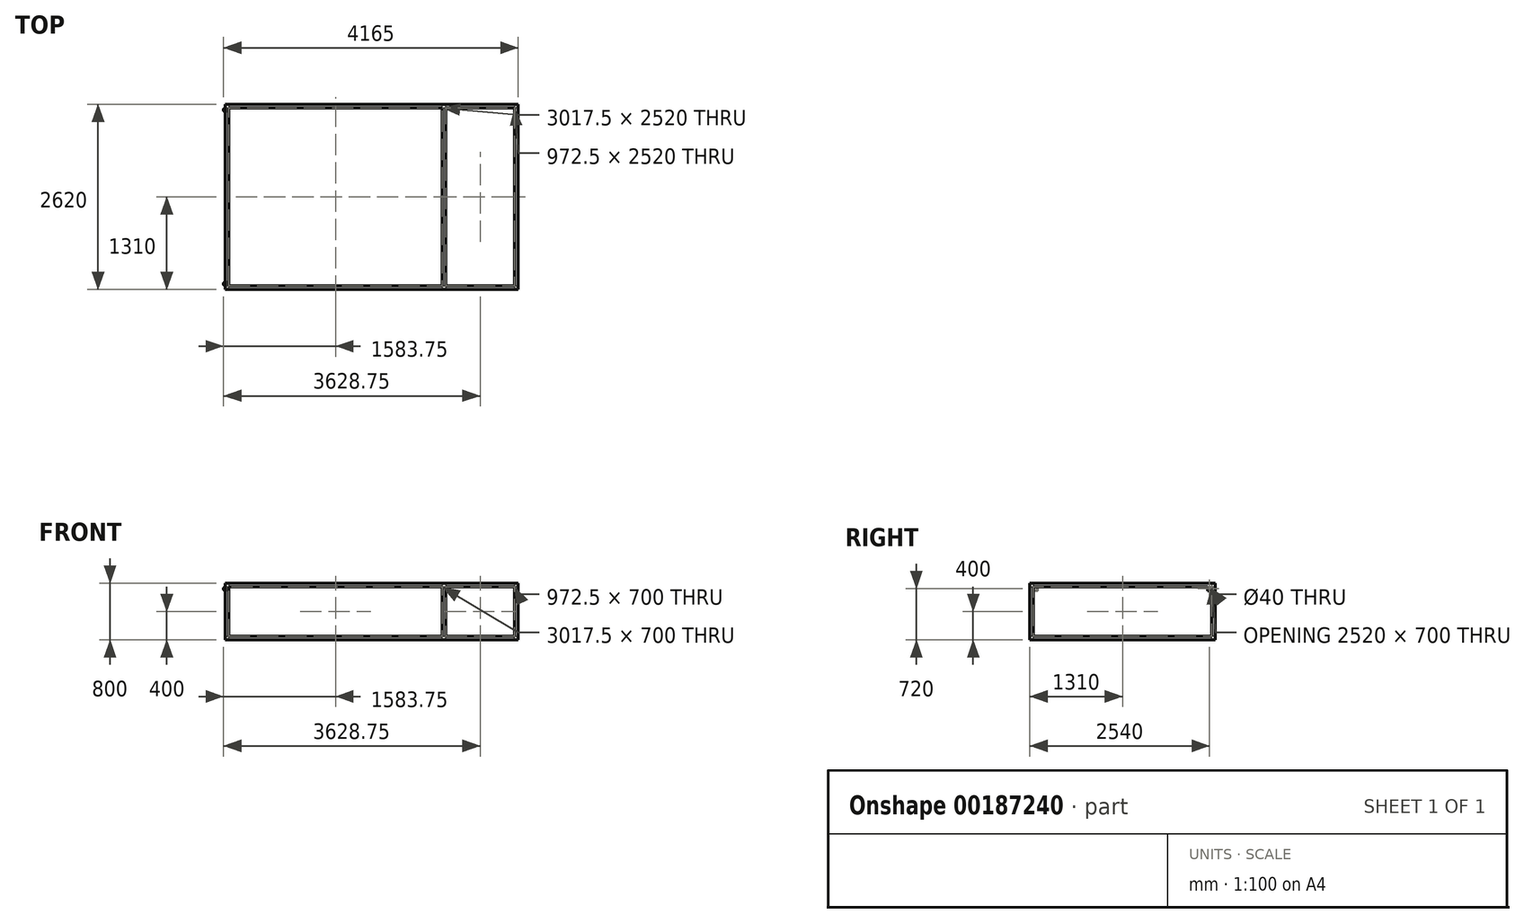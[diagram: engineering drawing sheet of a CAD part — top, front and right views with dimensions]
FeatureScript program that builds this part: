
annotation { "Feature Type Name" : "Feature", "Feature Type Description" : "" }
export const myFeature = defineFeature(function(context is Context, id is Id, definition is map)
    precondition{}
    {
        {
            var Q0;
            Q0=qCreatedBy(makeId("Top.planeOp"),FACE);
            var sketch = newSketch(context, id + "F0", { "sketchPlane" : qUnion([Q0])});
            skLineSegment(sketch, "E0.bottom", {"start": v(2070, 1310) * mm, "end": v(-2070, 1310) * mm});
            skLineSegment(sketch, "E0.top", {"start": v(2070, -1310) * mm, "end": v(-2070, -1310) * mm});
            skLineSegment(sketch, "E0.left", {"start": v(2070, 1310) * mm, "end": v(2070, -1310) * mm});
            skLineSegment(sketch, "E0.right", {"start": v(-2070, 1310) * mm, "end": v(-2070, -1310) * mm});
            skPoint(sketch, "E0.middle", {"position": v(0, 0) * mm});
            skLineSegment(sketch, "E1.bottom", {"start": v(2020, 1260) * mm, "end": v(-2020, 1260) * mm});
            skLineSegment(sketch, "E1.top", {"start": v(2020, -1260) * mm, "end": v(-2020, -1260) * mm});
            skLineSegment(sketch, "E1.left", {"start": v(2020, 1260) * mm, "end": v(2020, -1260) * mm});
            skLineSegment(sketch, "E1.right", {"start": v(-2020, 1260) * mm, "end": v(-2020, -1260) * mm});
            skLineSegment(sketch, "E2.bottom", {"start": v(-1047.5, 1260) * mm, "end": v(-997.5, 1260) * mm});
            skLineSegment(sketch, "E2.top", {"start": v(-1047.5, -1260) * mm, "end": v(-997.5, -1260) * mm});
            skLineSegment(sketch, "E2.left", {"start": v(-1047.5, 1260) * mm, "end": v(-1047.5, -1260) * mm});
            skLineSegment(sketch, "E2.right", {"start": v(-997.5, 1260) * mm, "end": v(-997.5, -1260) * mm});
            skLineSegment(sketch, "E3.bottom", {"start": v(-25, 1260) * mm, "end": v(25, 1260) * mm});
            skLineSegment(sketch, "E3.top", {"start": v(-25, -1260) * mm, "end": v(25, -1260) * mm});
            skLineSegment(sketch, "E3.left", {"start": v(-25, 1260) * mm, "end": v(-25, -1260) * mm});
            skLineSegment(sketch, "E3.right", {"start": v(25, 1260) * mm, "end": v(25, -1260) * mm});
            skLineSegment(sketch, "E4", {"start": v(997.5, 1260) * mm, "end": v(997.5, -1260) * mm});
            skLineSegment(sketch, "E5", {"start": v(1047.5, 1260) * mm, "end": v(1047.5, -1260) * mm});
            skSolve(sketch);
        }
        {
            var Q0;
            Q0=makeQuery(id+"F0.imprint","IMPRINT",FACE,{"disambiguationData":[TD([[makeQuery(id+"F0.imprint","IMPRINT",EDGE,{"derivedFrom":sQuery(id+"F0.wireOp",EDGE,"E2.bottom")}),-1.0]])]});
            var Q1;
            Q1=makeQuery(id+"F0.imprint","IMPRINT",FACE,{"disambiguationData":[TD([[makeQuery(id+"F0.imprint","IMPRINT",EDGE,{"derivedFrom":sQuery(id+"F0.wireOp",EDGE,"E3.bottom")}),-1.0]])]});
            var Q2;
            Q2=makeQuery(id+"F0.imprint","IMPRINT",FACE,{"disambiguationData":[TD([[makeQuery(id+"F0.imprint","IMPRINT",EDGE,{"derivedFrom":sQuery(id+"F0.wireOp",EDGE,"E0.bottom")}),1.0]])]});
            var Q3;
            Q3=makeQuery(id+"F0.imprint","IMPRINT",FACE,{"disambiguationData":[TD([[makeQuery(id+"F0.imprint","IMPRINT",EDGE,{"derivedFrom":sQuery(id+"F0.wireOp",EDGE,"jgCyhH8V-Kqar-OWqv-ijgf-Kz5bHVKDnid5.bottom")}),-1.0]])]});
            var Q4;
            Q4=makeQuery(id+"F0.imprint","IMPRINT",FACE,{"disambiguationData":[TD([[makeQuery(id+"F0.imprint","IMPRINT",EDGE,{"derivedFrom":sQuery(id+"F0.wireOp",EDGE,"XhDMClVQ-WPul-xyTN-NVR5-pGDVUJ7XdDNI.bottom")}),-1.0]])]});
            var Q5;
            Q5=makeQuery(id+"F0.imprint","IMPRINT",FACE,{"disambiguationData":[TD([[makeQuery(id+"F0.imprint","IMPRINT",EDGE,{"derivedFrom":sQuery(id+"F0.wireOp",EDGE,"bqqU8GJv-TmUe-bIrR-hqwj-hyhpdHZhHJpy.bottom")}),-1.0]])]});
            var Q6;
            Q6=makeQuery(id+"F0.imprint","IMPRINT",FACE,{"disambiguationData":[TD([[makeQuery(id+"F0.imprint","IMPRINT",EDGE,{"derivedFrom":sQuery(id+"F0.wireOp",EDGE,"7Y8udR0j-65Si-q316-6p89-ioPUt3QmM6FG.bottom")}),-1.0]])]});
            var Q7;
            Q7=makeQuery(id+"F0.imprint","IMPRINT",FACE,{"disambiguationData":[TD([[makeQuery(id+"F0.imprint","IMPRINT",EDGE,{"derivedFrom":sQuery(id+"F0.wireOp",EDGE,"J5J7LRau-4C0N-kJxE-FYC5-iCK4to3PdZMN.bottom")}),-1.0]])]});
            var Q8;
            {var subQ0=sQuery(id+"F0.wireOp",EDGE,"E4");Q8=makeQuery(id+"F0.imprint","IMPRINT",FACE,{"disambiguationData":[TD([[makeQuery(id+"F0.imprint","IMPRINT",EDGE,{"derivedFrom":subQ0}),1.0]])]});}
            extrude(context, id + "F1", {"entities" : qUnion([Q0, Q1, Q2, Q3, Q4, Q5, Q6, Q7, Q8]), "oppositeDirection" : true, "depth" : 50 * mm});
        }
        {
            var Q0;
            Q0=makeQuery(id+"F1.opExtrude","CAP_FACE",FACE,{"disambiguationData":[OSD([sQuery(id+"F0.wireOp",EDGE,"E0.bottom"),sQuery(id+"F0.wireOp",EDGE,"E0.top"),sQuery(id+"F0.wireOp",EDGE,"E0.left"),sQuery(id+"F0.wireOp",EDGE,"E0.right"),sQuery(id+"F0.wireOp",EDGE,"E1.bottom"),sQuery(id+"F0.wireOp",EDGE,"E1.top"),sQuery(id+"F0.wireOp",EDGE,"E1.left"),sQuery(id+"F0.wireOp",EDGE,"E1.right"),sQuery(id+"F0.wireOp",EDGE,"E2.left"),sQuery(id+"F0.wireOp",EDGE,"E2.right"),sQuery(id+"F0.wireOp",EDGE,"E3.left"),sQuery(id+"F0.wireOp",EDGE,"E3.right"),sQuery(id+"F0.wireOp",EDGE,"E4"),sQuery(id+"F0.wireOp",EDGE,"E5")])],"isStart":true});
            var sketch = newSketch(context, id + "F2", { "sketchPlane" : qUnion([Q0])});
            skLineSegment(sketch, "E6.bottom", {"start": v(-1047.5, 1260) * mm, "end": v(-997.5, 1260) * mm});
            skLineSegment(sketch, "E6.top", {"start": v(-1047.5, 1310) * mm, "end": v(-997.5, 1310) * mm});
            skLineSegment(sketch, "E6.left", {"start": v(-1047.5, 1260) * mm, "end": v(-1047.5, 1310) * mm});
            skLineSegment(sketch, "E6.right", {"start": v(-997.5, 1260) * mm, "end": v(-997.5, 1310) * mm});
            skLineSegment(sketch, "E7.bottom", {"start": v(-25, 1260) * mm, "end": v(25, 1260) * mm});
            skLineSegment(sketch, "E7.top", {"start": v(-25, 1310) * mm, "end": v(25, 1310) * mm});
            skLineSegment(sketch, "E7.left", {"start": v(-25, 1260) * mm, "end": v(-25, 1310) * mm});
            skLineSegment(sketch, "E7.right", {"start": v(25, 1260) * mm, "end": v(25, 1310) * mm});
            skLineSegment(sketch, "E8.bottom", {"start": v(997.5, 1260) * mm, "end": v(1047.5, 1260) * mm});
            skLineSegment(sketch, "E8.top", {"start": v(997.5, 1310) * mm, "end": v(1047.5, 1310) * mm});
            skLineSegment(sketch, "E8.left", {"start": v(997.5, 1260) * mm, "end": v(997.5, 1310) * mm});
            skLineSegment(sketch, "E8.right", {"start": v(1047.5, 1260) * mm, "end": v(1047.5, 1310) * mm});
            skLineSegment(sketch, "E9.bottom", {"start": v(2070, 1310) * mm, "end": v(2020, 1310) * mm});
            skLineSegment(sketch, "E9.top", {"start": v(2070, 1260) * mm, "end": v(2020, 1260) * mm});
            skLineSegment(sketch, "E9.left", {"start": v(2070, 1310) * mm, "end": v(2070, 1260) * mm});
            skLineSegment(sketch, "E9.right", {"start": v(2020, 1310) * mm, "end": v(2020, 1260) * mm});
            skLineSegment(sketch, "E10.bottom", {"start": v(-2070, 1310) * mm, "end": v(-2020, 1310) * mm});
            skLineSegment(sketch, "E10.top", {"start": v(-2070, 1260) * mm, "end": v(-2020, 1260) * mm});
            skLineSegment(sketch, "E10.left", {"start": v(-2070, 1310) * mm, "end": v(-2070, 1260) * mm});
            skLineSegment(sketch, "E10.right", {"start": v(-2020, 1310) * mm, "end": v(-2020, 1260) * mm});
            skLineSegment(sketch, "E11.bottom", {"start": v(-2070, -1310) * mm, "end": v(-2020, -1310) * mm});
            skLineSegment(sketch, "E11.top", {"start": v(-2070, -1260) * mm, "end": v(-2020, -1260) * mm});
            skLineSegment(sketch, "E11.left", {"start": v(-2070, -1310) * mm, "end": v(-2070, -1260) * mm});
            skLineSegment(sketch, "E11.right", {"start": v(-2020, -1310) * mm, "end": v(-2020, -1260) * mm});
            skLineSegment(sketch, "E12.bottom", {"start": v(-1047.5, -1260) * mm, "end": v(-997.5, -1260) * mm});
            skLineSegment(sketch, "E12.top", {"start": v(-1047.5, -1310) * mm, "end": v(-997.5, -1310) * mm});
            skLineSegment(sketch, "E12.left", {"start": v(-1047.5, -1260) * mm, "end": v(-1047.5, -1310) * mm});
            skLineSegment(sketch, "E12.right", {"start": v(-997.5, -1260) * mm, "end": v(-997.5, -1310) * mm});
            skLineSegment(sketch, "E13.bottom", {"start": v(-25, -1260) * mm, "end": v(25, -1260) * mm});
            skLineSegment(sketch, "E13.top", {"start": v(-25, -1310) * mm, "end": v(25, -1310) * mm});
            skLineSegment(sketch, "E13.left", {"start": v(-25, -1260) * mm, "end": v(-25, -1310) * mm});
            skLineSegment(sketch, "E13.right", {"start": v(25, -1260) * mm, "end": v(25, -1310) * mm});
            skLineSegment(sketch, "E14.bottom", {"start": v(997.5, -1260) * mm, "end": v(1047.5, -1260) * mm});
            skLineSegment(sketch, "E14.top", {"start": v(997.5, -1310) * mm, "end": v(1047.5, -1310) * mm});
            skLineSegment(sketch, "E14.left", {"start": v(997.5, -1260) * mm, "end": v(997.5, -1310) * mm});
            skLineSegment(sketch, "E14.right", {"start": v(1047.5, -1260) * mm, "end": v(1047.5, -1310) * mm});
            skLineSegment(sketch, "E15.bottom", {"start": v(2020, -1260) * mm, "end": v(2070, -1260) * mm});
            skLineSegment(sketch, "E15.top", {"start": v(2020, -1310) * mm, "end": v(2070, -1310) * mm});
            skLineSegment(sketch, "E15.left", {"start": v(2020, -1260) * mm, "end": v(2020, -1310) * mm});
            skLineSegment(sketch, "E15.right", {"start": v(2070, -1260) * mm, "end": v(2070, -1310) * mm});
            skSolve(sketch);
        }
        {
            var Q0;
            Q0=makeQuery(id+"F2.imprint","IMPRINT",FACE,{"disambiguationData":[TD([[makeQuery(id+"F2.imprint","IMPRINT",EDGE,{"derivedFrom":sQuery(id+"F2.wireOp",EDGE,"E10.bottom")}),1.0]])]});
            var Q1;
            Q1=makeQuery(id+"F2.imprint","IMPRINT",FACE,{"disambiguationData":[TD([[makeQuery(id+"F2.imprint","IMPRINT",EDGE,{"derivedFrom":sQuery(id+"F2.wireOp",EDGE,"E6.bottom")}),1.0]])]});
            var Q2;
            Q2=makeQuery(id+"F2.imprint","IMPRINT",FACE,{"disambiguationData":[TD([[makeQuery(id+"F2.imprint","IMPRINT",EDGE,{"derivedFrom":sQuery(id+"F2.wireOp",EDGE,"E7.bottom")}),1.0]])]});
            var Q3;
            Q3=makeQuery(id+"F2.imprint","IMPRINT",FACE,{"disambiguationData":[TD([[makeQuery(id+"F2.imprint","IMPRINT",EDGE,{"derivedFrom":sQuery(id+"F2.wireOp",EDGE,"E8.bottom")}),1.0]])]});
            var Q4;
            Q4=makeQuery(id+"F2.imprint","IMPRINT",FACE,{"disambiguationData":[TD([[makeQuery(id+"F2.imprint","IMPRINT",EDGE,{"derivedFrom":sQuery(id+"F2.wireOp",EDGE,"E9.bottom")}),1.0]])]});
            var Q5;
            Q5=makeQuery(id+"F2.imprint","IMPRINT",FACE,{"disambiguationData":[TD([[makeQuery(id+"F2.imprint","IMPRINT",EDGE,{"derivedFrom":sQuery(id+"F2.wireOp",EDGE,"E15.bottom")}),-1.0]])]});
            var Q6;
            Q6=makeQuery(id+"F2.imprint","IMPRINT",FACE,{"disambiguationData":[TD([[makeQuery(id+"F2.imprint","IMPRINT",EDGE,{"derivedFrom":sQuery(id+"F2.wireOp",EDGE,"E14.bottom")}),-1.0]])]});
            var Q7;
            Q7=makeQuery(id+"F2.imprint","IMPRINT",FACE,{"disambiguationData":[TD([[makeQuery(id+"F2.imprint","IMPRINT",EDGE,{"derivedFrom":sQuery(id+"F2.wireOp",EDGE,"E13.bottom")}),-1.0]])]});
            var Q8;
            Q8=makeQuery(id+"F2.imprint","IMPRINT",FACE,{"disambiguationData":[TD([[makeQuery(id+"F2.imprint","IMPRINT",EDGE,{"derivedFrom":sQuery(id+"F2.wireOp",EDGE,"E12.bottom")}),-1.0]])]});
            var Q9;
            Q9=makeQuery(id+"F2.imprint","IMPRINT",FACE,{"disambiguationData":[TD([[makeQuery(id+"F2.imprint","IMPRINT",EDGE,{"derivedFrom":sQuery(id+"F2.wireOp",EDGE,"E11.bottom")}),-1.0]])]});
            extrude(context, id + "F3", {"entities" : qUnion([Q0, Q1, Q2, Q3, Q4, Q5, Q6, Q7, Q8, Q9]), "operationType" : NewBodyOperationType.ADD, "depth" : 700 * mm});
        }
        {
            var Q0;
            Q0=makeQuery(id+"F3.opExtrude","SWEPT_EDGE",EDGE,{"disambiguationData":[OSD([sQuery(id+"F0.wireOp",EDGE,"E0.left"),sQuery(id+"F2.wireOp",EDGE,"E15.bottom"),sQuery(id+"F2.wireOp",EDGE,"E15.right")])]});
            cPoint(context, id + "F4", {"entities" : qUnion([Q0]), "parameter" : 0.5});
        }
        {
            var Q0;
            Q0=qCreatedBy(makeId("Top.planeOp"),FACE);
            var Q1;
            Q1 = qCreatedBy(id + "F4" ,VERTEX);
            cPlane(context, id + "F5", {"entities" : qUnion([Q0, Q1]), "cplaneType" : CPlaneType.PLANE_POINT, "offset" : 25 * mm, "width" : 150 * mm, "height" : 150 * mm});
        }
        {
            var Q0;
            Q0=makeQuery(id+"F1.opExtrude","SWEPT_BODY",BODY,{"disambiguationData":[OSD([sQuery(id+"F0.wireOp",EDGE,"E0.bottom"),sQuery(id+"F0.wireOp",EDGE,"E0.top"),sQuery(id+"F0.wireOp",EDGE,"E0.left"),sQuery(id+"F0.wireOp",EDGE,"E0.right"),sQuery(id+"F0.wireOp",EDGE,"E1.bottom"),sQuery(id+"F0.wireOp",EDGE,"E1.top"),sQuery(id+"F0.wireOp",EDGE,"E1.left"),sQuery(id+"F0.wireOp",EDGE,"E1.right"),sQuery(id+"F0.wireOp",EDGE,"E2.left"),sQuery(id+"F0.wireOp",EDGE,"E2.right"),sQuery(id+"F0.wireOp",EDGE,"E3.left"),sQuery(id+"F0.wireOp",EDGE,"E3.right"),sQuery(id+"F0.wireOp",EDGE,"E4"),sQuery(id+"F0.wireOp",EDGE,"E5")])]});
            var Q1;
            Q1=qCreatedBy(id+"F5.planeOp",FACE);
            mirror(context, id + "F6", {"operationType" : NewBodyOperationType.ADD, "entities" : qUnion([Q0]), "mirrorPlane" : qUnion([Q1])});
        }
        {
            var Q0;
            {var subQ0=makeQuery(id+"F3.boolean.opBoolean","MERGE",FACE,{"derivedFrom":[makeQuery(id+"F1.opExtrude","SWEPT_FACE",FACE,{"disambiguationData":[OSD([sQuery(id+"F0.wireOp",EDGE,"E0.left")])]}),makeQuery(id+"F3.opExtrude","SWEPT_FACE",FACE,{"disambiguationData":[OSD([sQuery(id+"F2.wireOp",EDGE,"E9.left")])]}),makeQuery(id+"F3.opExtrude","SWEPT_FACE",FACE,{"disambiguationData":[OSD([sQuery(id+"F2.wireOp",EDGE,"E15.right")])]})]});Q0=makeQuery(id+"F6.boolean.opBoolean","MERGE",FACE,{"derivedFrom":[subQ0,makeQuery(id+"F6.opPattern","COPY",FACE,{"derivedFrom":subQ0,"instanceName":"1"})]});}
            var sketch = newSketch(context, id + "F7", { "sketchPlane" : qUnion([Q0])});
            skLineSegment(sketch, "E16.bottom", {"start": v(1260, 700) * mm, "end": v(1200, 700) * mm});
            skLineSegment(sketch, "E16.top", {"start": v(1260, 640) * mm, "end": v(1200, 640) * mm});
            skLineSegment(sketch, "E16.left", {"start": v(1260, 700) * mm, "end": v(1260, 640) * mm});
            skLineSegment(sketch, "E16.right", {"start": v(1200, 700) * mm, "end": v(1200, 640) * mm});
            skLineSegment(sketch, "E17.bottom", {"start": v(-1260, 700) * mm, "end": v(-1200, 700) * mm});
            skLineSegment(sketch, "E17.top", {"start": v(-1260, 640) * mm, "end": v(-1200, 640) * mm});
            skLineSegment(sketch, "E17.left", {"start": v(-1260, 700) * mm, "end": v(-1260, 640) * mm});
            skLineSegment(sketch, "E17.right", {"start": v(-1200, 700) * mm, "end": v(-1200, 640) * mm});
            skCircle(sketch, "E18", {"center": v(-1230, 670) * mm, "radius": 20 * mm});
            skPoint(sketch, "E18.centerSnap0", {"position": v(-1200, 670) * mm});
            skPoint(sketch, "E18.centerSnap1", {"position": v(-1230, 640) * mm});
            skCircle(sketch, "E19", {"center": v(1230, 670) * mm, "radius": 20 * mm});
            skPoint(sketch, "E19.centerSnap0", {"position": v(1200, 670) * mm});
            skPoint(sketch, "E19.centerSnap1", {"position": v(1230, 640) * mm});
            skSolve(sketch);
        }
        {
            var Q0;
            Q0=makeQuery(id+"F7.imprint","IMPRINT",FACE,{"disambiguationData":[TD([[makeQuery(id+"F7.imprint","IMPRINT",EDGE,{"derivedFrom":sQuery(id+"F7.wireOp",EDGE,"E17.bottom")}),1.0]])]});
            var Q1;
            Q1=makeQuery(id+"F7.imprint","IMPRINT",FACE,{"disambiguationData":[TD([[makeQuery(id+"F7.imprint","IMPRINT",EDGE,{"derivedFrom":sQuery(id+"F7.wireOp",EDGE,"E16.bottom")}),1.0]])]});
            extrude(context, id + "F8", {"entities" : qUnion([Q0, Q1]), "operationType" : NewBodyOperationType.ADD, "oppositeDirection" : true, "depth" : 10 * mm});
        }
        {
            var Q0;
            {var subQ0=makeQuery(id+"F3.boolean.opBoolean","MERGE",FACE,{"derivedFrom":[makeQuery(id+"F1.opExtrude","SWEPT_FACE",FACE,{"disambiguationData":[OSD([sQuery(id+"F0.wireOp",EDGE,"E0.right")])]}),makeQuery(id+"F3.opExtrude","SWEPT_FACE",FACE,{"disambiguationData":[OSD([sQuery(id+"F2.wireOp",EDGE,"E10.left")])]}),makeQuery(id+"F3.opExtrude","SWEPT_FACE",FACE,{"disambiguationData":[OSD([sQuery(id+"F2.wireOp",EDGE,"E11.left")])]})]});Q0=makeQuery(id+"F6.boolean.opBoolean","MERGE",FACE,{"derivedFrom":[subQ0,makeQuery(id+"F6.opPattern","COPY",FACE,{"derivedFrom":subQ0,"instanceName":"1"})]});}
            var sketch = newSketch(context, id + "F9", { "sketchPlane" : qUnion([Q0])});
            skLineSegment(sketch, "E20.bottom", {"start": v(-1260, 700) * mm, "end": v(-1200, 700) * mm});
            skLineSegment(sketch, "E20.top", {"start": v(-1260, 640) * mm, "end": v(-1200, 640) * mm});
            skLineSegment(sketch, "E20.left", {"start": v(-1260, 700) * mm, "end": v(-1260, 640) * mm});
            skLineSegment(sketch, "E20.right", {"start": v(-1200, 700) * mm, "end": v(-1200, 640) * mm});
            skLineSegment(sketch, "E21.bottom", {"start": v(1260, 700) * mm, "end": v(1200, 700) * mm});
            skLineSegment(sketch, "E21.top", {"start": v(1260, 640) * mm, "end": v(1200, 640) * mm});
            skLineSegment(sketch, "E21.left", {"start": v(1260, 700) * mm, "end": v(1260, 640) * mm});
            skLineSegment(sketch, "E21.right", {"start": v(1200, 700) * mm, "end": v(1200, 640) * mm});
            skCircle(sketch, "E22", {"center": v(1230, 670) * mm, "radius": 18.5 * mm});
            skPoint(sketch, "E22.centerSnap0", {"position": v(1200, 670) * mm});
            skPoint(sketch, "E22.centerSnap1", {"position": v(1230, 640) * mm});
            skCircle(sketch, "E23", {"center": v(-1230, 670) * mm, "radius": 18.5 * mm});
            skPoint(sketch, "E23.centerSnap0", {"position": v(-1230, 640) * mm});
            skPoint(sketch, "E23.centerSnap1", {"position": v(-1200, 670) * mm});
            skSolve(sketch);
        }
        {
            var Q0;
            Q0 = qSketchRegion(id + "F9", true);
            var Q1;
            Q1=makeQuery(id+"F9.imprint","IMPRINT",FACE,{"disambiguationData":[TD([[makeQuery(id+"F9.imprint","IMPRINT",EDGE,{"derivedFrom":sQuery(id+"F9.wireOp",EDGE,"E22")}),1.0]])]});
            var Q2;
            Q2=makeQuery(id+"F9.imprint","IMPRINT",FACE,{"disambiguationData":[TD([[makeQuery(id+"F9.imprint","IMPRINT",EDGE,{"derivedFrom":sQuery(id+"F9.wireOp",EDGE,"E23")}),1.0]])]});
            extrude(context, id + "F10", {"entities" : qUnion([Q0, Q1, Q2]), "oppositeDirection" : true, "depth" : 25 * mm});
        }
        {
            var Q0;
            Q0=makeQuery(id+"F9.imprint","IMPRINT",FACE,{"disambiguationData":[TD([[makeQuery(id+"F9.imprint","IMPRINT",EDGE,{"derivedFrom":sQuery(id+"F9.wireOp",EDGE,"E23")}),1.0]])]});
            var Q1;
            Q1=makeQuery(id+"F9.imprint","IMPRINT",FACE,{"disambiguationData":[TD([[makeQuery(id+"F9.imprint","IMPRINT",EDGE,{"derivedFrom":sQuery(id+"F9.wireOp",EDGE,"E22")}),1.0]])]});
            extrude(context, id + "F11", {"entities" : qUnion([Q0, Q1]), "depth" : 25 * mm});
        }
        {
            var Q0;
            Q0=makeQuery(id+"F11.opExtrude","CAP_EDGE",EDGE,{"disambiguationData":[OSD([sQuery(id+"F9.wireOp",EDGE,"E23")])],"isStart":false});
            var Q1;
            Q1=makeQuery(id+"F11.opExtrude","CAP_EDGE",EDGE,{"disambiguationData":[OSD([sQuery(id+"F9.wireOp",EDGE,"E22")])],"isStart":false});
            fillet(context, id + "F12", {"entities" : qUnion([Q0, Q1]), "radius" : 7 * mm, "tangentPropagation" : true, "allowEdgeOverflow" : false});
        }
    });
